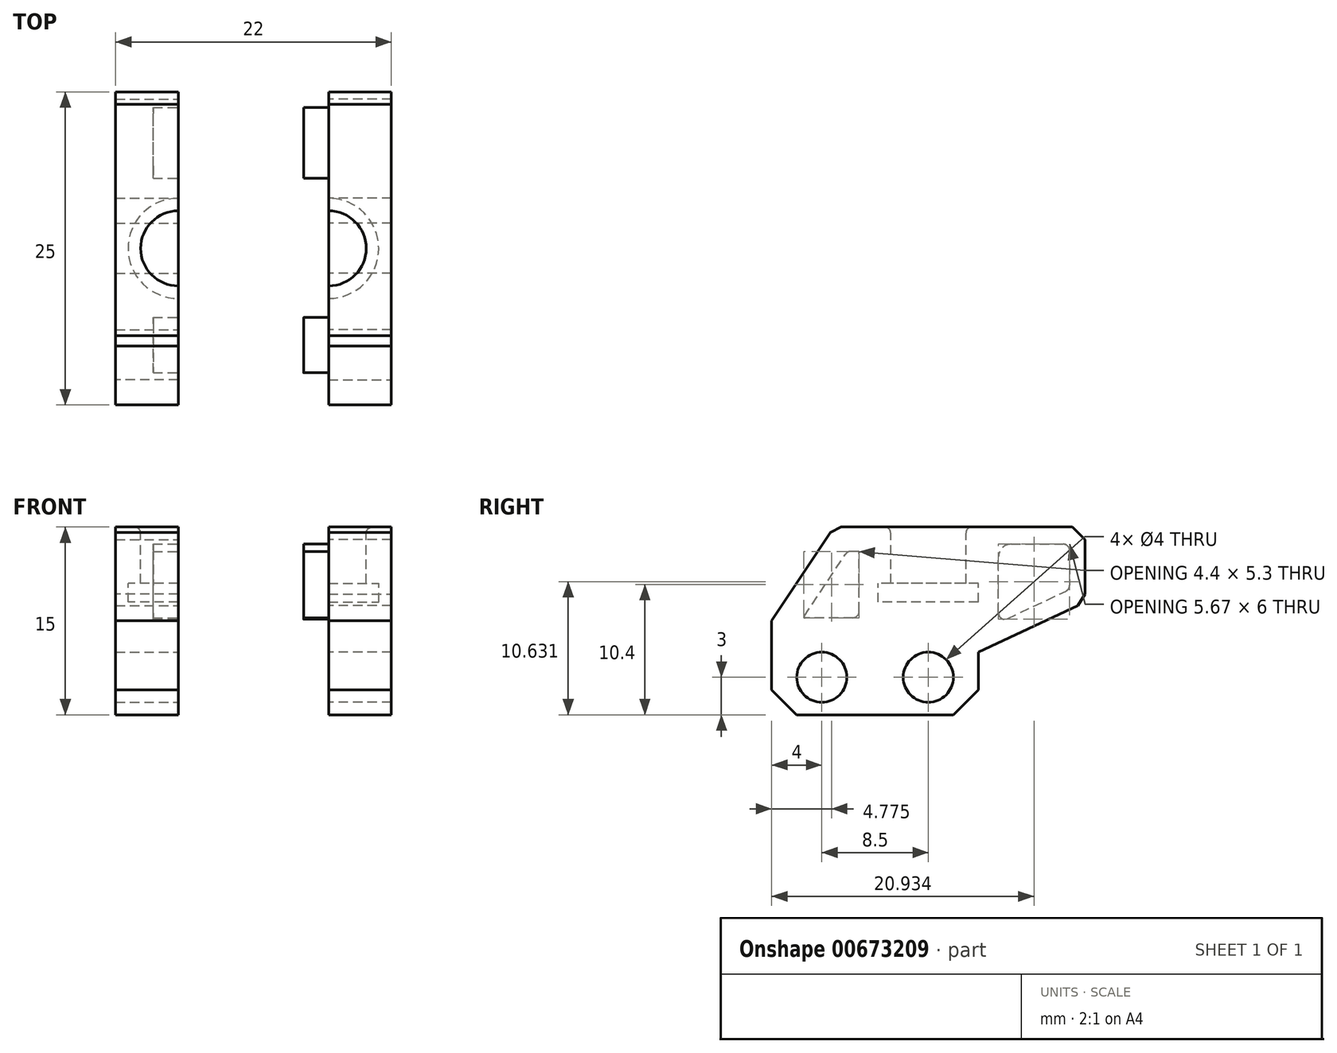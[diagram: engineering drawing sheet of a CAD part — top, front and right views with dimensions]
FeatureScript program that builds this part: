
annotation { "Feature Type Name" : "Feature", "Feature Type Description" : "" }
export const myFeature = defineFeature(function(context is Context, id is Id, definition is map)
    precondition{}
    {
        {
            var Q0;
            Q0=qCreatedBy(makeId("Right.planeOp"),FACE);
            var sketch = newSketch(context, id + "F0", { "sketchPlane" : qUnion([Q0])});
            skLineSegment(sketch, "E0.bottom", {"start": v(0, 15) * mm, "end": v(-15, 15) * mm});
            skLineSegment(sketch, "E0.top", {"start": v(-3.5, 0) * mm, "end": v(-15, 0) * mm});
            skLineSegment(sketch, "E0.left", {"start": v(0, 15) * mm, "end": v(0, 6.65) * mm});
            skLineSegment(sketch, "E1", {"start": v(-7.5, 15) * mm, "end": v(-7.5, 9) * mm, "construction": true});
            skLineSegment(sketch, "E2", {"start": v(-7.5, 9) * mm, "end": v(-11.5, 9) * mm, "construction": true});
            skLineSegment(sketch, "E3", {"start": v(-11.5, 9) * mm, "end": v(-11.5, 10.5) * mm, "construction": true});
            skLineSegment(sketch, "E4", {"start": v(-11.5, 10.5) * mm, "end": v(-10.5, 10.5) * mm, "construction": true});
            skLineSegment(sketch, "E5", {"start": v(-10.5, 10.5) * mm, "end": v(-10.5, 15) * mm, "construction": true});
            skLineSegment(sketch, "E6.MirrorCS", {"start": v(-3.5, 9) * mm, "end": v(-3.5, 10.5) * mm, "construction": true});
            skLineSegment(sketch, "E7.MirrorCS", {"start": v(-7.5, 9) * mm, "end": v(-3.5, 9) * mm, "construction": true});
            skLineSegment(sketch, "E8.MirrorCS", {"start": v(-3.5, 10.5) * mm, "end": v(-4.5, 10.5) * mm, "construction": true});
            skLineSegment(sketch, "E9.MirrorCS", {"start": v(-4.5, 10.5) * mm, "end": v(-4.5, 15) * mm, "construction": true});
            skLineSegment(sketch, "E10", {"start": v(0, 15) * mm, "end": v(5, 15) * mm});
            skLineSegment(sketch, "E11", {"start": v(5, 15) * mm, "end": v(5, 9) * mm});
            skPoint(sketch, "E11.endSnap0", {"position": v(0, 7.5) * mm});
            skLineSegment(sketch, "E12", {"start": v(-15, 0) * mm, "end": v(-20, 0) * mm});
            skLineSegment(sketch, "E13", {"start": v(-20, 0) * mm, "end": v(-20, 7.5) * mm});
            skPoint(sketch, "E13.endSnap0", {"position": v(-15, 7.5) * mm});
            skLineSegment(sketch, "E14", {"start": v(-20, 7.5) * mm, "end": v(-15, 15) * mm});
            skLineSegment(sketch, "E15", {"start": v(-3.5, 0) * mm, "end": v(-3.5, 5) * mm});
            skLineSegment(sketch, "E16", {"start": v(-3.5, 5) * mm, "end": v(5, 9) * mm});
            skPoint(sketch, "E17.orphan", {"position": v(5, 7.5) * mm});
            skPoint(sketch, "E18.orphan", {"position": v(0, 0) * mm});
            skLineSegment(sketch, "E19", {"start": v(-15, 15) * mm, "end": v(-15, 13.84) * mm, "construction": true});
            skSolve(sketch);
        }
        {
            var Q0;
            Q0=qSketchRegion(id+"F0",true);
            extrude(context, id + "F1", {"entities" : qUnion([Q0]), "oppositeDirection" : true, "depth" : 5 * mm});
        }
        {
            var Q0;
            Q0=makeQuery(id+"F1.opExtrude","SWEPT_FACE",FACE,{"disambiguationData":[OSD([sQuery(id+"F0.wireOp",EDGE,"E0.bottom"),sQuery(id+"F0.wireOp",EDGE,"E10")])]});
            var sketch = newSketch(context, id + "F2", { "sketchPlane" : qUnion([Q0])});
            skLineSegment(sketch, "E20", {"start": v(0, -15) * mm, "end": v(0, -7.5) * mm, "construction": true});
            skArc(sketch, "E21", {"start": v(0, -3.5) * mm, "mid": v(-4, -7.5) * mm, "end": v(0, -11.5) * mm});
            skArc(sketch, "E22", {"start": v(0, -4.5) * mm, "mid": v(-3, -7.5) * mm, "end": v(0, -10.5) * mm});
            skLineSegment(sketch, "E23", {"start": v(0, -3.5) * mm, "end": v(0, -11.5) * mm});
            skSolve(sketch);
        }
        {
            var Q0;
            {var subQ0=sQuery(id+"F2.wireOp",EDGE,"E21");Q0=makeQuery(id+"F2.imprint","IMPRINT",FACE,{"disambiguationData":[TD([[makeQuery(id+"F2.imprint","IMPRINT",EDGE,{"derivedFrom":subQ0}),1.0]])]});}
            var Q1;
            {var subQ0=sQuery(id+"F2.wireOp",EDGE,"E22");Q1=makeQuery(id+"F2.imprint","IMPRINT",FACE,{"disambiguationData":[TD([[makeQuery(id+"F2.imprint","IMPRINT",EDGE,{"derivedFrom":subQ0}),1.0]])]});}
            extrude(context, id + "F3", {"entities" : qUnion([Q0, Q1]), "operationType" : NewBodyOperationType.REMOVE, "oppositeDirection" : true, "depth" : 6 * mm});
        }
        {
            var Q0;
            {var subQ0=sQuery(id+"F2.wireOp",EDGE,"E21");Q0=makeQuery(id+"F2.imprint","IMPRINT",FACE,{"disambiguationData":[TD([[makeQuery(id+"F2.imprint","IMPRINT",EDGE,{"derivedFrom":subQ0}),1.0]])]});}
            extrude(context, id + "F4", {"entities" : qUnion([Q0]), "operationType" : NewBodyOperationType.ADD, "oppositeDirection" : true, "depth" : 4.5 * mm});
        }
        {
            var Q0;
            Q0=makeQuery(id+"F4.opExtrude","CAP_EDGE",EDGE,{"disambiguationData":[OSD([sQuery(id+"F2.wireOp",EDGE,"E22")])],"isStart":true});
            fillet(context, id + "F5", {"entities" : qUnion([Q0]), "radius" : .5 * mm, "tangentPropagation" : true, "allowEdgeOverflow" : false});
        }
        {
            var Q0;
            {var subQ0=sQuery(id+"F2.wireOp",EDGE,"E23");var subQ2=sQuery(id+"F0.wireOp",EDGE,"E10");var subQ3=sQuery(id+"F0.wireOp",EDGE,"E0.bottom");var subQ5=sQuery(id+"F2.wireOp",EDGE,"E22");Q0=makeQuery(id+"F4.boolean.opBoolean","MERGE",FACE,{"derivedFrom":[makeQuery(id+"F1.opExtrude","CAP_FACE",FACE,{"disambiguationData":[OSD([subQ3,sQuery(id+"F0.wireOp",EDGE,"E0.top"),subQ2,sQuery(id+"F0.wireOp",EDGE,"E11"),sQuery(id+"F0.wireOp",EDGE,"E12"),sQuery(id+"F0.wireOp",EDGE,"E13"),sQuery(id+"F0.wireOp",EDGE,"E14"),sQuery(id+"F0.wireOp",EDGE,"E15"),sQuery(id+"F0.wireOp",EDGE,"E16")])],"isStart":true}),makeQuery(id+"F4.opExtrude","SWEPT_FACE",FACE,{"disambiguationData":[OSD([subQ0]),TDD([makeQuery(id+"F2.imprint","IMPRINT",EDGE,{"disambiguationData":[TD([[makeQuery(id+"F2.imprint","INTERSECT",VERTEX,{"disambiguationData":[OD(0.0)],"derivedFrom":[subQ5,subQ0]}),1.0]])],"derivedFrom":subQ0})])]}),makeQuery(id+"F4.opExtrude","SWEPT_FACE",FACE,{"disambiguationData":[OSD([subQ0]),TDD([makeQuery(id+"F2.imprint","IMPRINT",EDGE,{"disambiguationData":[TD([[makeQuery(id+"F2.imprint","INTERSECT",VERTEX,{"disambiguationData":[OD(1.0)],"derivedFrom":[subQ5,subQ0]}),-1.0]])],"derivedFrom":subQ0})])]})]});}
            var sketch = newSketch(context, id + "F6", { "sketchPlane" : qUnion([Q0])});
            skLineSegment(sketch, "E24", {"start": v(-20, 0) * mm, "end": v(-20, 5) * mm, "construction": true});
            skLineSegment(sketch, "E25", {"start": v(-20, 5) * mm, "end": v(-3.5, 5) * mm, "construction": true});
            skLineSegment(sketch, "E26", {"start": v(-11.5, 9) * mm, "end": v(-11.5, 15) * mm, "construction": true});
            skLineSegment(sketch, "E27", {"start": v(-3.5, 9) * mm, "end": v(-3.5, 15) * mm, "construction": true});
            skLineSegment(sketch, "E28", {"start": v(-3.5, 15) * mm, "end": v(5, 15) * mm, "construction": true});
            skLineSegment(sketch, "E29", {"start": v(-11.5, 15) * mm, "end": v(-15, 15) * mm, "construction": true});
            skLineSegment(sketch, "E30", {"start": v(-20, 5) * mm, "end": v(-20, 7.5) * mm, "construction": true});
            skLineSegment(sketch, "E31.3", {"start": v(3.77, 13.13) * mm, "end": v(3.77, 10.33) * mm});
            skLineSegment(sketch, "E31.4", {"start": v(-0.9, 13.63) * mm, "end": v(3.27, 13.63) * mm});
            skLineSegment(sketch, "E31.5", {"start": v(-1.9, 8.13) * mm, "end": v(-1.9, 12.63) * mm});
            skLineSegment(sketch, "E32.trimOffspring", {"start": v(-1.19, 7.68) * mm, "end": v(3.48, 9.88) * mm});
            skLineSegment(sketch, "E33.0", {"start": v(-13.02, 8.25) * mm, "end": v(-13.02, 12.98) * mm});
            skLineSegment(sketch, "E33.1", {"start": v(-13.52, 7.75) * mm, "end": v(-17.35, 7.75) * mm});
            skLineSegment(sketch, "E33.2", {"start": v(-17.41, 7.87) * mm, "end": v(-14.1, 12.83) * mm});
            skLineSegment(sketch, "E33.3", {"start": v(-13.1, 13.05) * mm, "end": v(-13.69, 13.05) * mm});
            skPoint(sketch, "E34.visualSharp", {"position": v(-1.9, 7.34) * mm});
            skArc(sketch, "E34.filletArc", {"start": v(-1.9, 8.13) * mm, "mid": v(-1.67, 7.7) * mm, "end": v(-1.19, 7.68) * mm});
            skPoint(sketch, "E35.visualSharp", {"position": v(-1.9, 13.63) * mm});
            skArc(sketch, "E35.filletArc", {"start": v(-0.9, 13.63) * mm, "mid": v(-1.6, 13.34) * mm, "end": v(-1.9, 12.63) * mm});
            skPoint(sketch, "E36.visualSharp", {"position": v(3.77, 13.63) * mm});
            skArc(sketch, "E36.filletArc", {"start": v(3.77, 13.13) * mm, "mid": v(3.62, 13.48) * mm, "end": v(3.27, 13.63) * mm});
            skPoint(sketch, "E37.visualSharp", {"position": v(3.77, 10.01) * mm});
            skArc(sketch, "E37.filletArc", {"start": v(3.48, 9.88) * mm, "mid": v(3.69, 10.06) * mm, "end": v(3.77, 10.33) * mm});
            skPoint(sketch, "E38.visualSharp", {"position": v(-13.96, 13.05) * mm});
            skArc(sketch, "E38.filletArc", {"start": v(-13.69, 13.05) * mm, "mid": v(-13.92, 13) * mm, "end": v(-14.1, 12.83) * mm});
            skPoint(sketch, "E39.visualSharp", {"position": v(-13.02, 13.05) * mm});
            skArc(sketch, "E39.filletArc", {"start": v(-13.02, 12.98) * mm, "mid": v(-13.05, 13.03) * mm, "end": v(-13.1, 13.05) * mm});
            skPoint(sketch, "E40.visualSharp", {"position": v(-13.02, 7.75) * mm});
            skArc(sketch, "E40.filletArc", {"start": v(-13.52, 7.75) * mm, "mid": v(-13.17, 7.9) * mm, "end": v(-13.02, 8.25) * mm});
            skPoint(sketch, "E41.visualSharp", {"position": v(-17.49, 7.75) * mm});
            skArc(sketch, "E41.filletArc", {"start": v(-17.41, 7.87) * mm, "mid": v(-17.42, 7.79) * mm, "end": v(-17.35, 7.75) * mm});
            skCircle(sketch, "E42", {"center": v(-16, 3) * mm, "radius": 2 * mm});
            skCircle(sketch, "E43", {"center": v(-7.5, 3) * mm, "radius": 2 * mm});
            skLineSegment(sketch, "E44", {"start": v(-16, 3) * mm, "end": v(-7.5, 3) * mm, "construction": true});
            skSolve(sketch);
        }
        {
            var Q0;
            Q0=makeQuery(id+"F6.imprint","IMPRINT",FACE,{"disambiguationData":[TD([[makeQuery(id+"F6.imprint","IMPRINT",EDGE,{"derivedFrom":sQuery(id+"F6.wireOp",EDGE,"E33.0")}),1.0]])]});
            var Q1;
            Q1=makeQuery(id+"F6.imprint","IMPRINT",FACE,{"disambiguationData":[TD([[makeQuery(id+"F6.imprint","IMPRINT",EDGE,{"derivedFrom":sQuery(id+"F6.wireOp",EDGE,"E31.3")}),-1.0]])]});
            extrude(context, id + "F7", {"entities" : qUnion([Q0, Q1]), "operationType" : NewBodyOperationType.REMOVE, "oppositeDirection" : true, "depth" : 2 * mm});
        }
        {
            var Q0;
            Q0=makeQuery(id+"F6.imprint","IMPRINT",FACE,{"disambiguationData":[TD([[makeQuery(id+"F6.imprint","IMPRINT",EDGE,{"derivedFrom":sQuery(id+"F6.wireOp",EDGE,"E42")}),1.0]])]});
            var Q1;
            Q1=makeQuery(id+"F6.imprint","IMPRINT",FACE,{"disambiguationData":[TD([[makeQuery(id+"F6.imprint","IMPRINT",EDGE,{"derivedFrom":sQuery(id+"F6.wireOp",EDGE,"E43")}),1.0]])]});
            extrude(context, id + "F8", {"entities" : qUnion([Q0, Q1]), "operationType" : NewBodyOperationType.REMOVE, "oppositeDirection" : true, "depth" : 25 * mm});
        }
        {
            var Q0;
            Q0=makeQuery(id+"F1.opExtrude","SWEPT_EDGE",EDGE,{"disambiguationData":[OSD([sQuery(id+"F0.wireOp",EDGE,"E12"),sQuery(id+"F0.wireOp",EDGE,"E13")])]});
            var Q1;
            Q1=makeQuery(id+"F1.opExtrude","SWEPT_EDGE",EDGE,{"disambiguationData":[OSD([sQuery(id+"F0.wireOp",EDGE,"E0.top"),sQuery(id+"F0.wireOp",EDGE,"E15")])]});
            chamfer(context, id + "F9", {"entities" : qUnion([Q0, Q1]), "width" : 2 * mm, "tangentPropagation" : true});
        }
        {
            var Q0;
            Q0=makeQuery(id+"F1.opExtrude","SWEPT_EDGE",EDGE,{"disambiguationData":[OSD([sQuery(id+"F0.wireOp",EDGE,"E10"),sQuery(id+"F0.wireOp",EDGE,"E11")])]});
            var Q1;
            Q1=makeQuery(id+"F1.opExtrude","SWEPT_EDGE",EDGE,{"disambiguationData":[OSD([sQuery(id+"F0.wireOp",EDGE,"E11"),sQuery(id+"F0.wireOp",EDGE,"E16")])]});
            var Q2;
            Q2=makeQuery(id+"F1.opExtrude","SWEPT_EDGE",EDGE,{"disambiguationData":[OSD([sQuery(id+"F0.wireOp",EDGE,"E0.bottom"),sQuery(id+"F0.wireOp",EDGE,"E14")])]});
            chamfer(context, id + "F10", {"entities" : qUnion([Q0, Q1, Q2]), "width" : 1 * mm, "tangentPropagation" : true});
        }
        {
            var Q0;
            Q0=makeQuery(id+"F1.opExtrude","CAP_FACE",FACE,{"disambiguationData":[OSD([sQuery(id+"F0.wireOp",EDGE,"E0.bottom"),sQuery(id+"F0.wireOp",EDGE,"E0.top"),sQuery(id+"F0.wireOp",EDGE,"E10"),sQuery(id+"F0.wireOp",EDGE,"E11"),sQuery(id+"F0.wireOp",EDGE,"E12"),sQuery(id+"F0.wireOp",EDGE,"E13"),sQuery(id+"F0.wireOp",EDGE,"E14"),sQuery(id+"F0.wireOp",EDGE,"E15"),sQuery(id+"F0.wireOp",EDGE,"E16")])],"isStart":false});
            var sketch = newSketch(context, id + "F11", { "sketchPlane" : qUnion([Q0])});
            skLineSegment(sketch, "E45", {"start": v(5.23, 15) * mm, "end": v(4.23, 15) * mm, "construction": true});
            skLineSegment(sketch, "E46", {"start": v(4.23, 15) * mm, "end": v(4.23, 10.5) * mm, "construction": true});
            skCircle(sketch, "E47", {"center": v(4.23, 10.5) * mm, "radius": 3.5 * mm});
            skSolve(sketch);
        }
        {
            var Q0;
            Q0=makeQuery(id+"F2zs4y5K00VFYps_1.boolean.opBoolean","COPY",FACE,{"derivedFrom":makeQuery(id+"F2zs4y5K00VFYps_1.opExtrude","CAP_FACE",FACE,{"disambiguationData":[OSD([sQuery(id+"F11.wireOp",EDGE,"E47")])],"isStart":false})});
            var sketch = newSketch(context, id + "F12", { "sketchPlane" : qUnion([Q0])});
            skLineSegment(sketch, "E48", {"start": v(4.23, 10.5) * mm, "end": v(0.73, 10.5) * mm, "construction": true});
            skLineSegment(sketch, "E49", {"start": v(2.48, 13.53) * mm, "end": v(2.48, 7.47) * mm});
            skPoint(sketch, "E49.startSnap0", {"position": v(2.48, 10.5) * mm});
            skLineSegment(sketch, "E50", {"start": v(2.48, 10.5) * mm, "end": v(0.98, 10.5) * mm, "construction": true});
            skPoint(sketch, "E51.orphan", {"position": v(0.98, 11.8) * mm});
            skSolve(sketch);
        }
        {
            var Q0;
            Q0=qCreatedBy(makeId("Right.planeOp"),FACE);
            cPlane(context, id + "F13", {"entities" : qUnion([Q0]), "cplaneType" : CPlaneType.OFFSET, "offset" : 6 * mm, "width" : 150 * mm, "height" : 150 * mm});
        }
        {
            var Q0;
            Q0=makeQuery(id+"F1.opExtrude","SWEPT_BODY",BODY,{"disambiguationData":[OSD([sQuery(id+"F0.wireOp",EDGE,"E0.bottom"),sQuery(id+"F0.wireOp",EDGE,"E0.top"),sQuery(id+"F0.wireOp",EDGE,"E10"),sQuery(id+"F0.wireOp",EDGE,"E11"),sQuery(id+"F0.wireOp",EDGE,"E12"),sQuery(id+"F0.wireOp",EDGE,"E13"),sQuery(id+"F0.wireOp",EDGE,"E14"),sQuery(id+"F0.wireOp",EDGE,"E15"),sQuery(id+"F0.wireOp",EDGE,"E16")])]});
            var Q1;
            Q1=qCreatedBy(id+"F13.planeOp",FACE);
            mirror(context, id + "F14", {"entities" : qUnion([Q0]), "mirrorPlane" : qUnion([Q1])});
        }
        {
            var Q0;
            Q0=makeQuery(id+"F14.opPattern","COPY",FACE,{"derivedFrom":makeQuery(id+"F7.boolean.opBoolean","COPY",FACE,{"derivedFrom":makeQuery(id+"F7.opExtrude","CAP_FACE",FACE,{"disambiguationData":[OSD([sQuery(id+"F6.wireOp",EDGE,"E31.3"),sQuery(id+"F6.wireOp",EDGE,"E31.4"),sQuery(id+"F6.wireOp",EDGE,"E31.5"),sQuery(id+"F6.wireOp",EDGE,"E32.trimOffspring"),sQuery(id+"F6.wireOp",EDGE,"E34.filletArc"),sQuery(id+"F6.wireOp",EDGE,"E35.filletArc"),sQuery(id+"F6.wireOp",EDGE,"E36.filletArc"),sQuery(id+"F6.wireOp",EDGE,"E37.filletArc")])],"isStart":false})}),"instanceName":"1"});
            var Q1;
            Q1=makeQuery(id+"F14.opPattern","COPY",FACE,{"derivedFrom":makeQuery(id+"F7.boolean.opBoolean","COPY",FACE,{"derivedFrom":makeQuery(id+"F7.opExtrude","CAP_FACE",FACE,{"disambiguationData":[OSD([sQuery(id+"F6.wireOp",EDGE,"E33.0"),sQuery(id+"F6.wireOp",EDGE,"E33.1"),sQuery(id+"F6.wireOp",EDGE,"E33.2"),sQuery(id+"F6.wireOp",EDGE,"E33.3"),sQuery(id+"F6.wireOp",EDGE,"E38.filletArc"),sQuery(id+"F6.wireOp",EDGE,"E39.filletArc"),sQuery(id+"F6.wireOp",EDGE,"E40.filletArc"),sQuery(id+"F6.wireOp",EDGE,"E41.filletArc")])],"isStart":false})}),"instanceName":"1"});
            extrude(context, id + "F15", {"entities" : qUnion([Q0, Q1]), "operationType" : NewBodyOperationType.ADD, "depth" : 4 * mm});
        }
    });
